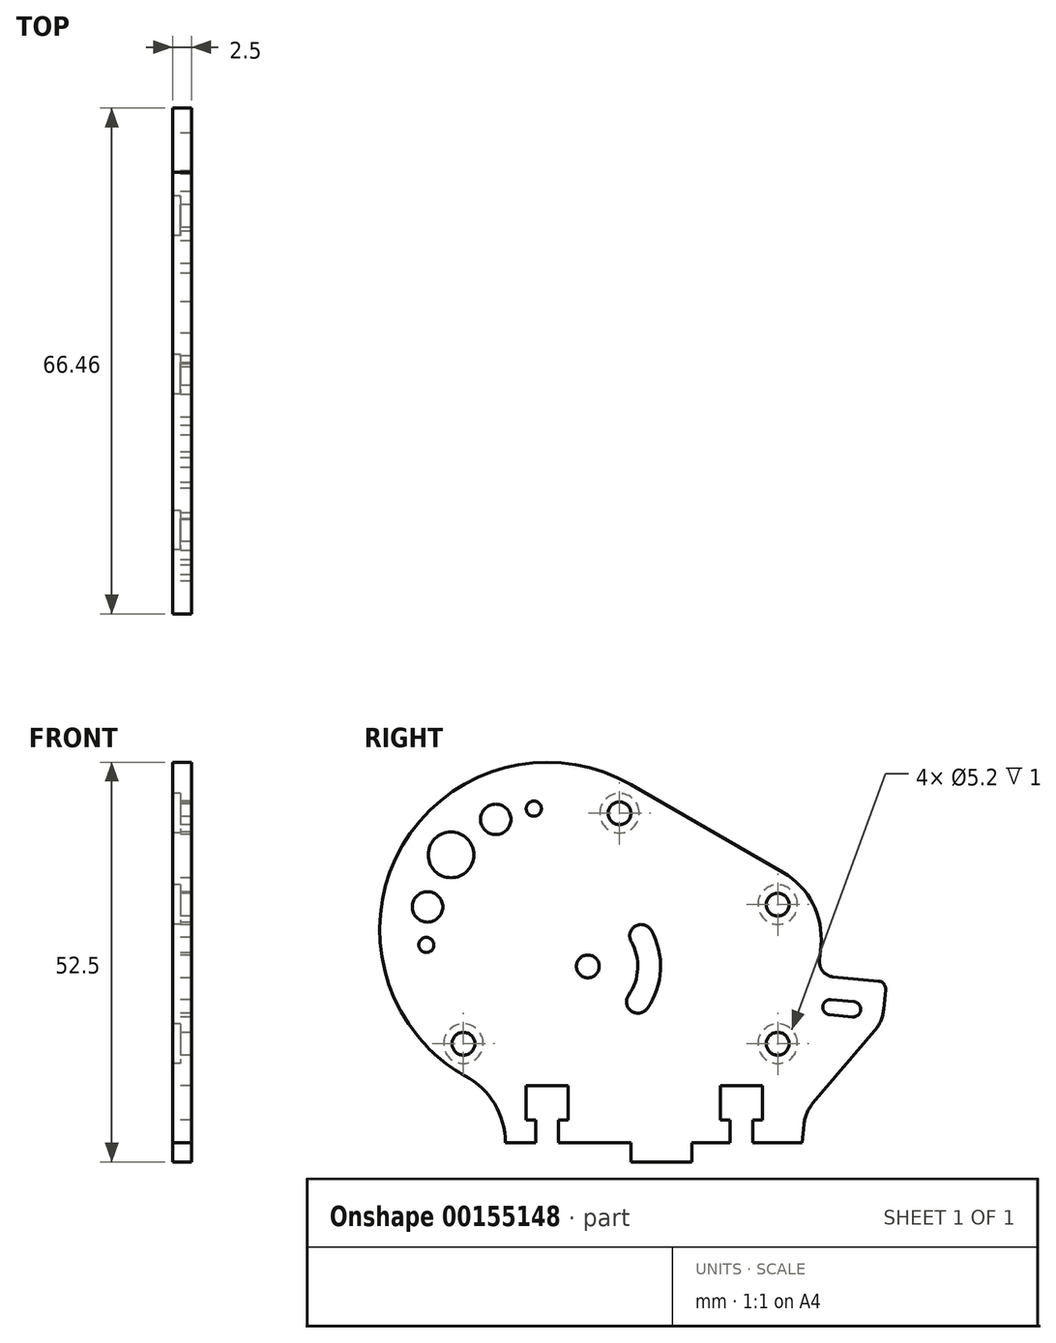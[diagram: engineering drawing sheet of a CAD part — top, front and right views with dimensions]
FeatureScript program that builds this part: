
annotation { "Feature Type Name" : "Feature", "Feature Type Description" : "" }
export const myFeature = defineFeature(function(context is Context, id is Id, definition is map)
    precondition{}
    {
        {
            var Q0;
            Q0=qCreatedBy(makeId("Right.planeOp"),FACE);
            var sketch = newSketch(context, id + "F0", { "sketchPlane" : qUnion([Q0])});
            skLineSegment(sketch, "E0.bottom", {"start": v(-19.5, 0) * mm, "end": v(-15.5, 0) * mm});
            skArc(sketch, "E1", {"start": v(-3, 47.05) * mm, "mid": v(-30.77, 42.24) * mm, "end": v(-31.02, 14.06) * mm});
            skArc(sketch, "E2", {"start": v(21.96, 25.9) * mm, "mid": v(20.89, 31.43) * mm, "end": v(17, 35.5) * mm});
            skLineSegment(sketch, "E3", {"start": v(-30.76, 13.75) * mm, "end": v(-31.02, 14.06) * mm});
            skLineSegment(sketch, "E4", {"start": v(-3, 47.05) * mm, "end": v(17, 35.5) * mm});
            skLineSegment(sketch, "E5", {"start": v(19.5, 0) * mm, "end": v(19.73, 2.43) * mm});
            skLineSegment(sketch, "E6.left", {"start": v(-15.5, 3) * mm, "end": v(-15.5, 0) * mm});
            skLineSegment(sketch, "E6.right", {"start": v(-12.5, 3) * mm, "end": v(-12.5, 0) * mm});
            skLineSegment(sketch, "E7.left", {"start": v(10, 3) * mm, "end": v(10, 0) * mm});
            skLineSegment(sketch, "E7.right", {"start": v(13, 3) * mm, "end": v(13, 0) * mm});
            skLineSegment(sketch, "E8.bottom", {"start": v(8.75, 7.5) * mm, "end": v(14.25, 7.5) * mm});
            skLineSegment(sketch, "E8.top", {"start": v(8.75, 3) * mm, "end": v(10, 3) * mm});
            skLineSegment(sketch, "E8.left", {"start": v(8.75, 7.5) * mm, "end": v(8.75, 3) * mm});
            skLineSegment(sketch, "E8.right", {"start": v(14.25, 7.5) * mm, "end": v(14.25, 3) * mm});
            skLineSegment(sketch, "E9.bottom", {"start": v(-16.75, 7.5) * mm, "end": v(-11.25, 7.5) * mm});
            skLineSegment(sketch, "E9.top", {"start": v(-16.75, 3) * mm, "end": v(-15.5, 3) * mm});
            skLineSegment(sketch, "E9.left", {"start": v(-16.75, 7.5) * mm, "end": v(-16.75, 3) * mm});
            skLineSegment(sketch, "E9.right", {"start": v(-11.25, 7.5) * mm, "end": v(-11.25, 3) * mm});
            skLineSegment(sketch, "E10.trimOffspring", {"start": v(-12.5, 3) * mm, "end": v(-11.25, 3) * mm});
            skLineSegment(sketch, "E11.trimOffspring", {"start": v(-12.5, 0) * mm, "end": v(-3, 0) * mm});
            skLineSegment(sketch, "E12.trimOffspring", {"start": v(13, 0) * mm, "end": v(19.5, 0) * mm});
            skLineSegment(sketch, "E13.trimOffspring", {"start": v(13, 3) * mm, "end": v(14.25, 3) * mm});
            skLineSegment(sketch, "E14", {"start": v(-14, 28) * mm, "end": v(0, 19.92) * mm, "construction": true});
            skLineSegment(sketch, "E15", {"start": v(-13.86, 26.19) * mm, "end": v(0, 18.19) * mm, "construction": true});
            skCircle(sketch, "E16", {"center": v(-8.66, 23.19) * mm, "radius": 1.5 * mm});
            skLineSegment(sketch, "E17.top", {"start": v(-3, -2.5) * mm, "end": v(5, -2.5) * mm});
            skLineSegment(sketch, "E17.left", {"start": v(-3, 0) * mm, "end": v(-3, -2.5) * mm});
            skLineSegment(sketch, "E17.right", {"start": v(5, 0) * mm, "end": v(5, -2.5) * mm});
            skLineSegment(sketch, "E18.trimOffspring", {"start": v(5, 0) * mm, "end": v(10, 0) * mm});
            skCircle(sketch, "E19", {"center": v(-4.5, 43.3) * mm, "radius": 1.5 * mm});
            skCircle(sketch, "E20", {"center": v(16.28, 31.3) * mm, "radius": 1.5 * mm});
            skCircle(sketch, "E21", {"center": v(-25, 13.02) * mm, "radius": 1.5 * mm});
            skCircle(sketch, "E22", {"center": v(16.28, 13.02) * mm, "radius": 1.5 * mm});
            skCircle(sketch, "E23", {"center": v(-14, 28) * mm, "radius": 16 * mm, "construction": true});
            skCircle(sketch, "E24", {"center": v(-26.62, 37.83) * mm, "radius": 3 * mm});
            skCircle(sketch, "E25", {"center": v(-20.76, 42.5) * mm, "radius": 2 * mm});
            skCircle(sketch, "E26", {"center": v(-29.72, 31) * mm, "radius": 2 * mm});
            skCircle(sketch, "E27", {"center": v(-29.87, 26) * mm, "radius": 1 * mm});
            skCircle(sketch, "E28", {"center": v(-15.76, 43.9) * mm, "radius": 1 * mm});
            skLineSegment(sketch, "E29", {"start": v(-14, 28) * mm, "end": v(-36, 28) * mm, "construction": true});
            skCircle(sketch, "E30", {"center": v(-8.66, 23.19) * mm, "radius": 8.06 * mm, "construction": true});
            skArc(sketch, "E31", {"start": v(-0.36, 27.93) * mm, "mid": v(-2.4, 28.49) * mm, "end": v(-2.96, 26.44) * mm});
            skArc(sketch, "E32", {"start": v(-3.3, 19.4) * mm, "mid": v(-2.94, 17.3) * mm, "end": v(-0.85, 17.67) * mm});
            skArc(sketch, "E33", {"start": v(-3.3, 19.4) * mm, "mid": v(-2.1, 22.87) * mm, "end": v(-2.96, 26.44) * mm});
            skArc(sketch, "E34", {"start": v(-0.85, 17.67) * mm, "mid": v(0.9, 22.73) * mm, "end": v(-0.36, 27.93) * mm});
            skLineSegment(sketch, "E35", {"start": v(-8.66, 23.19) * mm, "end": v(-1.66, 27.19) * mm, "construction": true});
            skLineSegment(sketch, "E36", {"start": v(-8.66, 23.19) * mm, "end": v(-2.08, 18.53) * mm, "construction": true});
            skLineSegment(sketch, "E37", {"start": v(23.58, 21.81) * mm, "end": v(29.55, 21.25) * mm});
            skLineSegment(sketch, "E38", {"start": v(30.45, 20.16) * mm, "end": v(30.2, 17.52) * mm});
            skLineSegment(sketch, "E39", {"start": v(29.03, 14.75) * mm, "end": v(20.9, 5.2) * mm});
            skLineSegment(sketch, "E40.trimOffspring", {"start": v(21.77, 24) * mm, "end": v(21.96, 25.9) * mm});
            skPoint(sketch, "E41.visualSharp", {"position": v(19.88, 4) * mm});
            skArc(sketch, "E41.filletArc", {"start": v(20.9, 5.2) * mm, "mid": v(20.1, 3.9) * mm, "end": v(19.73, 2.43) * mm});
            skPoint(sketch, "E42.visualSharp", {"position": v(21.59, 22) * mm});
            skArc(sketch, "E42.filletArc", {"start": v(21.77, 24) * mm, "mid": v(22.22, 22.53) * mm, "end": v(23.58, 21.81) * mm});
            skPoint(sketch, "E43.visualSharp", {"position": v(30.55, 21.15) * mm});
            skArc(sketch, "E43.filletArc", {"start": v(30.45, 20.16) * mm, "mid": v(30.23, 20.89) * mm, "end": v(29.55, 21.25) * mm});
            skPoint(sketch, "E44.visualSharp", {"position": v(30.05, 15.95) * mm});
            skArc(sketch, "E44.filletArc", {"start": v(29.03, 14.75) * mm, "mid": v(29.83, 16.04) * mm, "end": v(30.2, 17.52) * mm});
            skLineSegment(sketch, "E45", {"start": v(23.3, 18.82) * mm, "end": v(26.28, 18.54) * mm});
            skLineSegment(sketch, "E46", {"start": v(26.28, 18.54) * mm, "end": v(26.1, 16.55) * mm, "construction": true});
            skLineSegment(sketch, "E47", {"start": v(26.1, 16.55) * mm, "end": v(23.1, 16.83) * mm});
            skLineSegment(sketch, "E48", {"start": v(23.1, 16.83) * mm, "end": v(23.3, 18.82) * mm, "construction": true});
            skArc(sketch, "E49", {"start": v(23.3, 18.82) * mm, "mid": v(22.2, 17.92) * mm, "end": v(23.1, 16.83) * mm});
            skArc(sketch, "E50", {"start": v(26.1, 16.55) * mm, "mid": v(27.18, 17.45) * mm, "end": v(26.28, 18.54) * mm});
            skArc(sketch, "E51", {"start": v(-19.5, 0) * mm, "mid": v(-20.92, 5.13) * mm, "end": v(-24.76, 8.8) * mm});
            skPoint(sketch, "E52.visualSharp", {"position": v(-27.53, 9.8) * mm});
            skArc(sketch, "E52.filletArc", {"start": v(-30.76, 13.75) * mm, "mid": v(-28, 10.98) * mm, "end": v(-24.76, 8.8) * mm});
            skLineSegment(sketch, "E53", {"start": v(-8.66, 23.19) * mm, "end": v(6.34, 23.19) * mm, "construction": true});
            skSolve(sketch);
        }
        {
            var Q0;
            Q0=qSketchRegion(id+"F0",true);
            extrude(context, id + "F1", {"entities" : qUnion([Q0]), "depth" : 2.5 * mm});
        }
        {
            var Q0;
            Q0=makeQuery(id+"F1.opExtrude","CAP_FACE",FACE,{"disambiguationData":[OSD([sQuery(id+"F0.wireOp",EDGE,"E0.bottom"),sQuery(id+"F0.wireOp",EDGE,"E1"),sQuery(id+"F0.wireOp",EDGE,"E2"),sQuery(id+"F0.wireOp",EDGE,"E3"),sQuery(id+"F0.wireOp",EDGE,"E4"),sQuery(id+"F0.wireOp",EDGE,"E5"),sQuery(id+"F0.wireOp",EDGE,"E6.left"),sQuery(id+"F0.wireOp",EDGE,"E6.right"),sQuery(id+"F0.wireOp",EDGE,"E7.left"),sQuery(id+"F0.wireOp",EDGE,"E7.right"),sQuery(id+"F0.wireOp",EDGE,"E8.bottom"),sQuery(id+"F0.wireOp",EDGE,"E8.top"),sQuery(id+"F0.wireOp",EDGE,"E8.left"),sQuery(id+"F0.wireOp",EDGE,"E8.right"),sQuery(id+"F0.wireOp",EDGE,"E9.bottom"),sQuery(id+"F0.wireOp",EDGE,"E9.top"),sQuery(id+"F0.wireOp",EDGE,"E9.left"),sQuery(id+"F0.wireOp",EDGE,"E9.right"),sQuery(id+"F0.wireOp",EDGE,"E10.trimOffspring"),sQuery(id+"F0.wireOp",EDGE,"E11.trimOffspring"),sQuery(id+"F0.wireOp",EDGE,"E12.trimOffspring"),sQuery(id+"F0.wireOp",EDGE,"E13.trimOffspring"),sQuery(id+"F0.wireOp",EDGE,"E16"),sQuery(id+"F0.wireOp",EDGE,"E17.top"),sQuery(id+"F0.wireOp",EDGE,"E17.left"),sQuery(id+"F0.wireOp",EDGE,"E17.right"),sQuery(id+"F0.wireOp",EDGE,"E18.trimOffspring"),sQuery(id+"F0.wireOp",EDGE,"E19"),sQuery(id+"F0.wireOp",EDGE,"E20"),sQuery(id+"F0.wireOp",EDGE,"E21"),sQuery(id+"F0.wireOp",EDGE,"E22"),sQuery(id+"F0.wireOp",EDGE,"E24"),sQuery(id+"F0.wireOp",EDGE,"E25"),sQuery(id+"F0.wireOp",EDGE,"E26"),sQuery(id+"F0.wireOp",EDGE,"E27"),sQuery(id+"F0.wireOp",EDGE,"E28"),sQuery(id+"F0.wireOp",EDGE,"E31"),sQuery(id+"F0.wireOp",EDGE,"E32"),sQuery(id+"F0.wireOp",EDGE,"E33"),sQuery(id+"F0.wireOp",EDGE,"E34"),sQuery(id+"F0.wireOp",EDGE,"E37"),sQuery(id+"F0.wireOp",EDGE,"E38"),sQuery(id+"F0.wireOp",EDGE,"E39"),sQuery(id+"F0.wireOp",EDGE,"E40.trimOffspring"),sQuery(id+"F0.wireOp",EDGE,"E41.filletArc"),sQuery(id+"F0.wireOp",EDGE,"E42.filletArc"),sQuery(id+"F0.wireOp",EDGE,"E43.filletArc"),sQuery(id+"F0.wireOp",EDGE,"E44.filletArc"),sQuery(id+"F0.wireOp",EDGE,"E45"),sQuery(id+"F0.wireOp",EDGE,"E47"),sQuery(id+"F0.wireOp",EDGE,"E49"),sQuery(id+"F0.wireOp",EDGE,"E50"),sQuery(id+"F0.wireOp",EDGE,"E51"),sQuery(id+"F0.wireOp",EDGE,"E52.filletArc")])],"isStart":true});
            var sketch = newSketch(context, id + "F2", { "sketchPlane" : qUnion([Q0])});
            skCircle(sketch, "E54", {"center": v(4.5, 43.3) * mm, "radius": 2.6 * mm});
            skCircle(sketch, "E55", {"center": v(-16.28, 31.3) * mm, "radius": 2.6 * mm});
            skCircle(sketch, "E56", {"center": v(-16.28, 13.02) * mm, "radius": 2.6 * mm});
            skCircle(sketch, "E57", {"center": v(25, 13.02) * mm, "radius": 2.6 * mm});
            skSolve(sketch);
        }
        {
            var Q0;
            Q0 = qSketchRegion(id + "F2", true);
            extrude(context, id + "F3", {"entities" : qUnion([Q0]), "operationType" : NewBodyOperationType.REMOVE, "oppositeDirection" : true, "depth" : 1 * mm});
        }
    });
